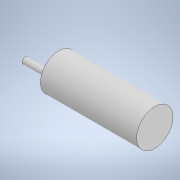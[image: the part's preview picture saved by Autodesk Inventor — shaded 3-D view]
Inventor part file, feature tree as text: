
AUTODESK INVENTOR PART (.ipt)
format: ipt  version: 2020.1 (Build 241239000, 239)  size: 112,640 bytes
history: native  units: mm
features: sketch x3, extrude x2, revolve x1
ambient origin geometry x8: Origin, YZ Plane, XZ Plane, XY Plane, X Axis, Y Axis, Z Axis, Center Point
bodies: Solid1 (feature_tree)
feature tree (6):
  revolve  "Revolution1"  [1 undecoded]
  extrude  "Extrusion3"  Depth=7.0mm
  extrude  "Extrusion4"  Depth=6.0mm
  sketch  "Sketch1"  dims[d13=90.0deg d30=97.8mm]
  sketch  "Sketch4"  dims[d31=7.0mm d32=12.0mm]
  sketch  "Sketch5"  dims[d33=7.0mm d34=0.0mm d35=6.0mm d36=27.0mm d37=0.0mm]
note: 1 required parameter value undecoded (feature->parameter linkage not recoverable at this tier; creation-order binding heuristic only, values carry confidence <= 0.55)
